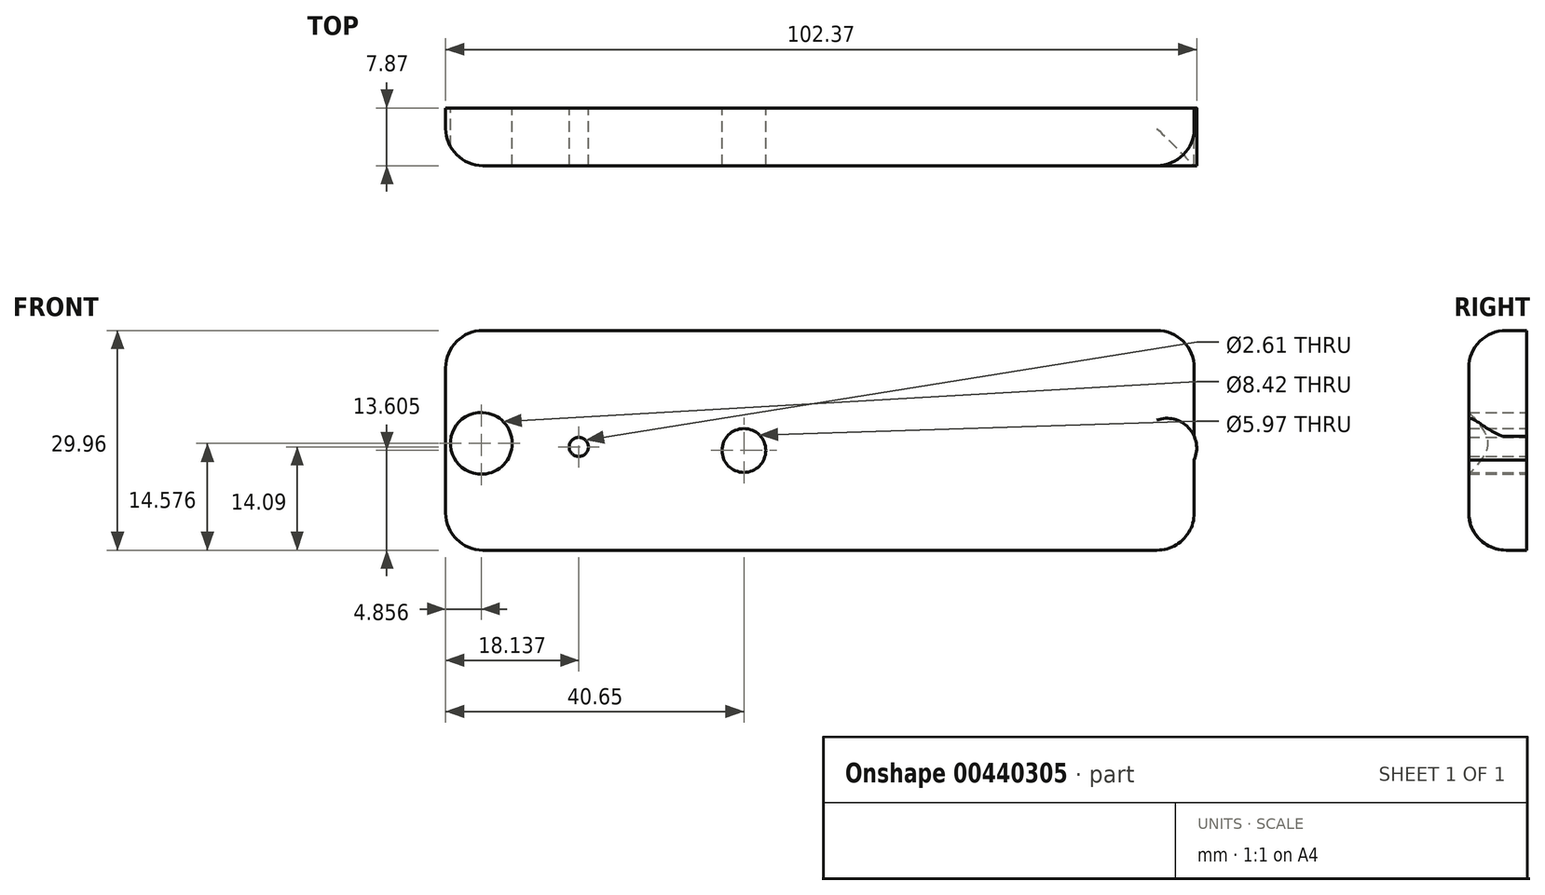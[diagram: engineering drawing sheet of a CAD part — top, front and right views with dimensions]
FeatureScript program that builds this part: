
annotation { "Feature Type Name" : "Feature", "Feature Type Description" : "" }
export const myFeature = defineFeature(function(context is Context, id is Id, definition is map)
    precondition{}
    {
        {
            var Q0;
            Q0=qCreatedBy(makeId("Front.planeOp"),FACE);
            var sketch = newSketch(context, id + "F0", { "sketchPlane" : qUnion([Q0])});
            skLineSegment(sketch, "E0.bottom", {"start": v(-40.65, 31.58) * mm, "end": v(61.38, 31.58) * mm});
            skLineSegment(sketch, "E0.top", {"start": v(-40.65, 1.62) * mm, "end": v(61.38, 1.62) * mm});
            skLineSegment(sketch, "E0.left", {"start": v(-40.65, 31.58) * mm, "end": v(-40.65, 1.62) * mm});
            skLineSegment(sketch, "E0.right", {"start": v(61.38, 31.58) * mm, "end": v(61.38, 1.62) * mm});
            skCircle(sketch, "E1", {"center": v(-35.8, 16.2) * mm, "radius": 4.21 * mm});
            skCircle(sketch, "E2", {"center": v(-22.51, 15.71) * mm, "radius": 1.3 * mm});
            skCircle(sketch, "E3", {"center": v(0, 15.22) * mm, "radius": 2.99 * mm});
            skCircle(sketch, "E4", {"center": v(57.66, 15.55) * mm, "radius": 4.06 * mm});
            skSolve(sketch);
        }
        {
            var Q0;
            Q0 = qSketchRegion(id + "F0", true);
            extrude(context, id + "F1", {"entities" : qUnion([Q0]), "depth" : 7.87 * mm});
        }
        {
            var Q0;
            Q0=makeQuery(id+"F1.opExtrude","SWEPT_EDGE",EDGE,{"disambiguationData":[OSD([sQuery(id+"F0.wireOp",EDGE,"E0.bottom"),sQuery(id+"F0.wireOp",EDGE,"E0.right")])]});
            var Q1;
            Q1=makeQuery(id+"F1.opExtrude","SWEPT_EDGE",EDGE,{"disambiguationData":[OSD([sQuery(id+"F0.wireOp",EDGE,"E0.bottom"),sQuery(id+"F0.wireOp",EDGE,"E0.left")])]});
            var Q2;
            Q2=makeQuery(id+"F1.opExtrude","SWEPT_EDGE",EDGE,{"disambiguationData":[OSD([sQuery(id+"F0.wireOp",EDGE,"E0.top"),sQuery(id+"F0.wireOp",EDGE,"E0.right")])]});
            var Q3;
            Q3=makeQuery(id+"F1.opExtrude","CAP_EDGE",EDGE,{"disambiguationData":[OSD([sQuery(id+"F0.wireOp",EDGE,"E0.top")])],"isStart":false});
            fillet(context, id + "F2", {"entities" : qUnion([Q0, Q1, Q2, Q3]), "radius" : 5.08 * mm, "tangentPropagation" : true, "allowEdgeOverflow" : false});
        }
        {
            var Q0;
            Q0=makeQuery(id+"F2.opFillet","BLEND_EDGE",EDGE,{"blendedFrom":[makeQuery(id+"F1.opExtrude","CAP_EDGE",EDGE,{"disambiguationData":[OSD([sQuery(id+"F0.wireOp",EDGE,"E0.top")])],"isStart":false}),makeQuery(id+"F1.opExtrude","SWEPT_FACE",FACE,{"disambiguationData":[OSD([sQuery(id+"F0.wireOp",EDGE,"E0.left")])]})],"blendedInto":[makeQuery(id+"F1.opExtrude","SWEPT_FACE",FACE,{"disambiguationData":[OSD([sQuery(id+"F0.wireOp",EDGE,"E0.left")])]})]});
            fillet(context, id + "F3", {"entities" : qUnion([Q0]), "radius" : 5.08 * mm, "tangentPropagation" : true, "allowEdgeOverflow" : false});
        }
    });
